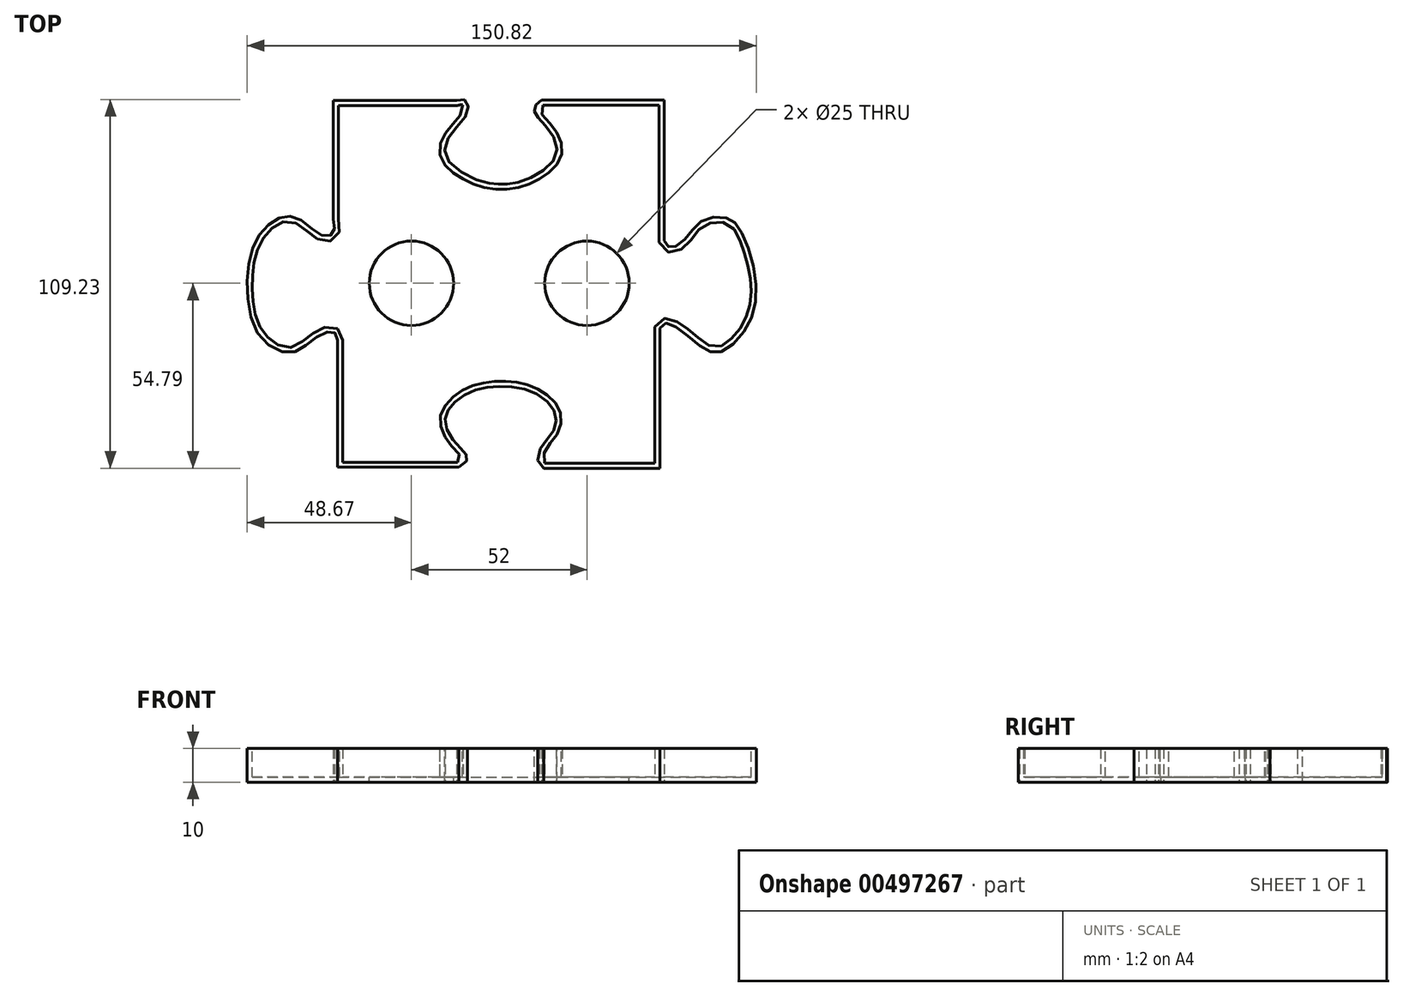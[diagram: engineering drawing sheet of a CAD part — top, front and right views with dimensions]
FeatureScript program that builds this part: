
annotation { "Feature Type Name" : "Feature", "Feature Type Description" : "" }
export const myFeature = defineFeature(function(context is Context, id is Id, definition is map)
    precondition{}
    {
        {
            var Q0;
            Q0=qCreatedBy(makeId("Top.planeOp"),FACE);
            var sketch = newSketch(context, id + "F0", { "sketchPlane" : qUnion([Q0])});
            skLineSegment(sketch, "E0", {"start": v(-49.12, 18.96) * mm, "end": v(-49.12, 54.17) * mm});
            skLineSegment(sketch, "E1", {"start": v(-49.12, 54.17) * mm, "end": v(-12.54, 54.17) * mm});
            skLineSegment(sketch, "E2", {"start": v(12.53, 54.22) * mm, "end": v(48.9, 54.22) * mm});
            skLineSegment(sketch, "E3", {"start": v(48.9, 54.22) * mm, "end": v(48.9, 12.66) * mm});
            skLineSegment(sketch, "E4", {"start": v(47.64, -13.27) * mm, "end": v(47.64, -54.8) * mm});
            skLineSegment(sketch, "E5", {"start": v(47.64, -54.8) * mm, "end": v(13.25, -54.8) * mm});
            skLineSegment(sketch, "E6", {"start": v(-11.98, -54.49) * mm, "end": v(-47.92, -54.49) * mm});
            skLineSegment(sketch, "E7", {"start": v(-47.92, -54.49) * mm, "end": v(-47.92, -16.88) * mm});
            skFitSpline(sketch, "E8", {"points": [v(-49.12, 18.96) * mm, v(-49.12, 14.98) * mm, v(-52.1, 14.05) * mm, v(-59.17, 18.96) * mm, v(-65.24, 19.34) * mm, v(-71.88, 12.93) * mm, v(-74.67, 0) * mm, v(-71.05, -15.48) * mm, v(-61.57, -20.5) * mm, v(-54.33, -16.04) * mm, v(-49.12, -14.4) * mm, v(-47.92, -16.88) * mm], "startDerivative": vector(13.24, -59.66) * mm, "endDerivative": vector(1.81, -67.74) * mm});
            skFitSpline(sketch, "E9", {"points": [v(-11.98, -54.49) * mm, v(-9.48, -51.42) * mm, v(-11.98, -48.36) * mm, v(-15.94, -41.71) * mm, v(-14.5, -36.66) * mm, v(-8.17, -32.04) * mm, v(0, -30.53) * mm, v(9.08, -31.85) * mm, v(16.1, -37.35) * mm, v(16.29, -43.23) * mm, v(12.12, -49.1) * mm, v(13.25, -54.8) * mm], "startDerivative": vector(80.82, 35) * mm, "endDerivative": vector(84, -23.8) * mm});
            skFitSpline(sketch, "E10", {"points": [v(47.64, -13.27) * mm, v(50.14, -11.86) * mm, v(58.5, -17.71) * mm, v(64.9, -20.5) * mm, v(73.17, -13.27) * mm, v(76.05, 0) * mm, v(71.65, 15.36) * mm, v(67.42, 19.34) * mm, v(59.51, 18.2) * mm, v(54.59, 12.51) * mm, v(50.42, 10.7) * mm, v(48.9, 12.66) * mm], "startDerivative": vector(32.29, 60.98) * mm, "endDerivative": vector(-39.33, 44.54) * mm});
            skFitSpline(sketch, "E11", {"points": [v(-12.54, 54.17) * mm, v(-9.99, 54.17) * mm, v(-9.5, 50.42) * mm, v(-14.8, 43.46) * mm, v(-15.29, 36.5) * mm, v(-4.85, 30.04) * mm, v(0, 29.38) * mm, v(4.59, 29.71) * mm, v(13.04, 33.36) * mm, v(17.18, 39.82) * mm, v(13.2, 47.27) * mm, v(10.6, 50.43) * mm, v(10.72, 52.57) * mm, v(12.53, 54.22) * mm], "startDerivative": vector(55.56, 13.73) * mm, "endDerivative": vector(43.1, 18.5) * mm});
            skSolve(sketch);
        }
        {
            var Q0;
            Q0=makeQuery(id+"F0.imprint","IMPRINT",FACE,{"disambiguationData":[TD([[makeQuery(id+"F0.imprint","IMPRINT",EDGE,{"derivedFrom":sQuery(id+"F0.wireOp",EDGE,"E0")}),-1.0]])]});
            extrude(context, id + "F1", {"entities" : qUnion([Q0]), "depth" : 10 * mm});
        }
        {
            var Q0;
            Q0=makeQuery(id+"F1.opExtrude","CAP_FACE",FACE,{"disambiguationData":[OSD([sQuery(id+"F0.wireOp",EDGE,"E0"),sQuery(id+"F0.wireOp",EDGE,"E1"),sQuery(id+"F0.wireOp",EDGE,"E2"),sQuery(id+"F0.wireOp",EDGE,"E3"),sQuery(id+"F0.wireOp",EDGE,"E4"),sQuery(id+"F0.wireOp",EDGE,"E5"),sQuery(id+"F0.wireOp",EDGE,"E6"),sQuery(id+"F0.wireOp",EDGE,"E7"),sQuery(id+"F0.wireOp",EDGE,"E8"),sQuery(id+"F0.wireOp",EDGE,"E9"),sQuery(id+"F0.wireOp",EDGE,"E10"),sQuery(id+"F0.wireOp",EDGE,"E11")])],"isStart":false});
            shell(context, id + "F2", {"entities" : qUnion([Q0]), "thickness" : 1.5 * mm});
        }
        {
            var Q0;
            Q0=makeQuery(id+"F2.opShell","OFFSET_FACE",FACE,{"disambiguationData":[OSD([sQuery(id+"F0.wireOp",EDGE,"E0"),sQuery(id+"F0.wireOp",EDGE,"E1"),sQuery(id+"F0.wireOp",EDGE,"E2"),sQuery(id+"F0.wireOp",EDGE,"E3"),sQuery(id+"F0.wireOp",EDGE,"E4"),sQuery(id+"F0.wireOp",EDGE,"E5"),sQuery(id+"F0.wireOp",EDGE,"E6"),sQuery(id+"F0.wireOp",EDGE,"E7"),sQuery(id+"F0.wireOp",EDGE,"E8"),sQuery(id+"F0.wireOp",EDGE,"E9"),sQuery(id+"F0.wireOp",EDGE,"E10"),sQuery(id+"F0.wireOp",EDGE,"E11")])]});
            var sketch = newSketch(context, id + "F3", { "sketchPlane" : qUnion([Q0])});
            skCircle(sketch, "E12", {"center": v(-26, 0) * mm, "radius": 12.5 * mm});
            skCircle(sketch, "E13", {"center": v(26, 0) * mm, "radius": 12.5 * mm});
            skSolve(sketch);
        }
        {
            var Q0;
            Q0=makeQuery(id+"F3.imprint","IMPRINT",FACE,{"disambiguationData":[TD([[makeQuery(id+"F3.imprint","IMPRINT",EDGE,{"derivedFrom":sQuery(id+"F3.wireOp",EDGE,"E12")}),1.0]])]});
            var Q1;
            Q1=makeQuery(id+"F3.imprint","IMPRINT",FACE,{"disambiguationData":[TD([[makeQuery(id+"F3.imprint","IMPRINT",EDGE,{"derivedFrom":sQuery(id+"F3.wireOp",EDGE,"E13")}),1.0]])]});
            extrude(context, id + "F4", {"entities" : qUnion([Q0, Q1]), "operationType" : NewBodyOperationType.REMOVE, "oppositeDirection" : true, "depth" : 25 * mm});
        }
    });
